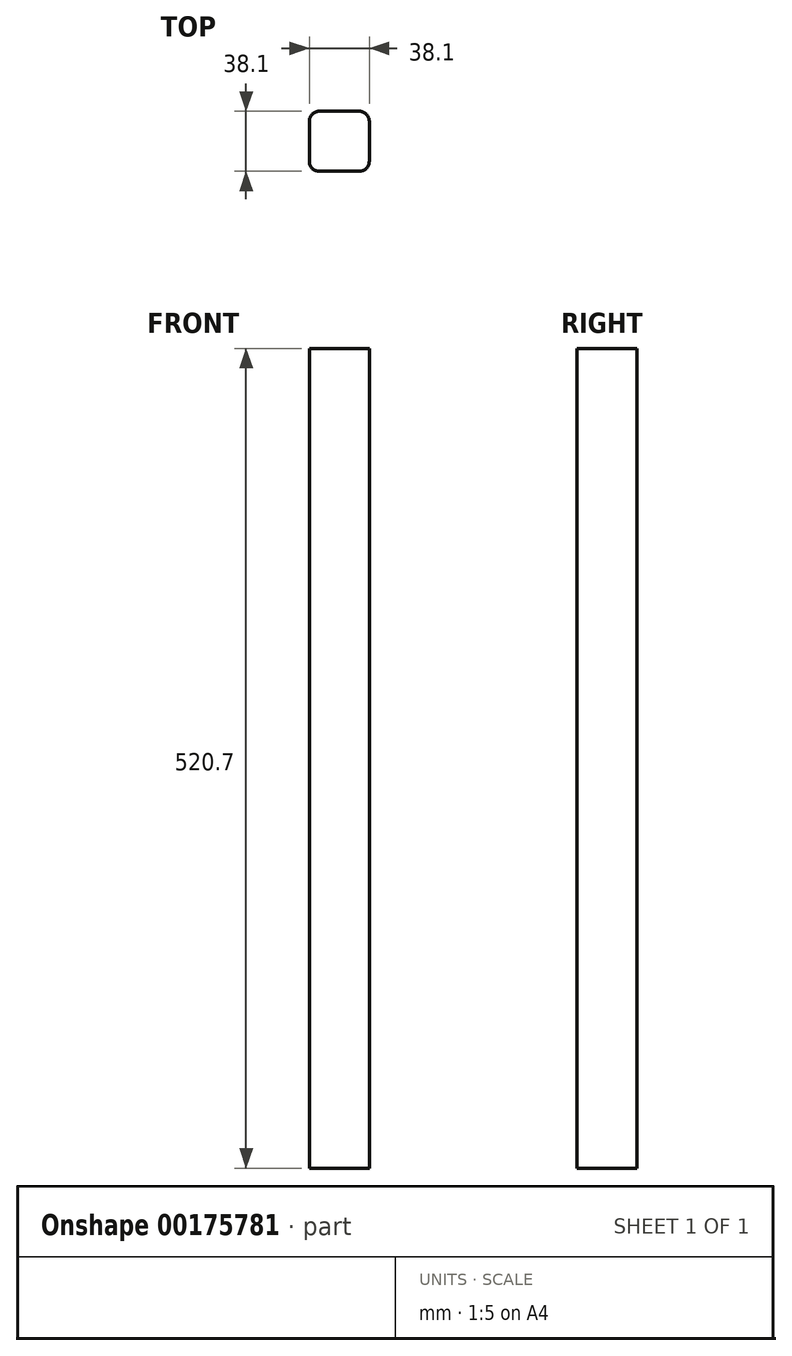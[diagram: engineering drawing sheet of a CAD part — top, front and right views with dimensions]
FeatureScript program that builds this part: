
annotation { "Feature Type Name" : "Feature", "Feature Type Description" : "" }
export const myFeature = defineFeature(function(context is Context, id is Id, definition is map)
    precondition{}
    {
        {
            var Q0;
            Q0=qCreatedBy(makeId("Top.planeOp"),FACE);
            var sketch = newSketch(context, id + "F0", { "sketchPlane" : qUnion([Q0])});
            skLineSegment(sketch, "E0.bottom", {"start": v(12.7, 19.05) * mm, "end": v(-12.7, 19.05) * mm});
            skLineSegment(sketch, "E0.top", {"start": v(12.7, -19.05) * mm, "end": v(-12.7, -19.05) * mm});
            skLineSegment(sketch, "E0.left", {"start": v(19.05, 12.7) * mm, "end": v(19.05, -12.7) * mm});
            skLineSegment(sketch, "E0.right", {"start": v(-19.05, 12.7) * mm, "end": v(-19.05, -12.7) * mm});
            skPoint(sketch, "E0.middle", {"position": v(0, 0) * mm});
            skPoint(sketch, "E1.visualSharp", {"position": v(-19.05, 19.05) * mm});
            skArc(sketch, "E1.filletArc", {"start": v(-12.7, 19.05) * mm, "mid": v(-17.2, 17.2) * mm, "end": v(-19.05, 12.7) * mm});
            skPoint(sketch, "E2.visualSharp", {"position": v(19.05, 19.05) * mm});
            skArc(sketch, "E2.filletArc", {"start": v(19.05, 12.7) * mm, "mid": v(17.2, 17.2) * mm, "end": v(12.7, 19.05) * mm});
            skPoint(sketch, "E3.visualSharp", {"position": v(19.05, -19.05) * mm});
            skArc(sketch, "E3.filletArc", {"start": v(12.7, -19.05) * mm, "mid": v(17.2, -17.2) * mm, "end": v(19.05, -12.7) * mm});
            skPoint(sketch, "E4.visualSharp", {"position": v(-19.05, -19.05) * mm});
            skArc(sketch, "E4.filletArc", {"start": v(-19.05, -12.7) * mm, "mid": v(-17.2, -17.2) * mm, "end": v(-12.7, -19.05) * mm});
            skSolve(sketch);
        }
        {
            var Q0;
            Q0=makeQuery(id+"F0.imprint","IMPRINT",FACE,{"disambiguationData":[TD([[makeQuery(id+"F0.imprint","IMPRINT",EDGE,{"derivedFrom":sQuery(id+"F0.wireOp",EDGE,"E0.bottom")}),1.0]])]});
            extrude(context, id + "F1", {"entities" : qUnion([Q0]), "depth" : 520.7 * mm});
        }
    });
